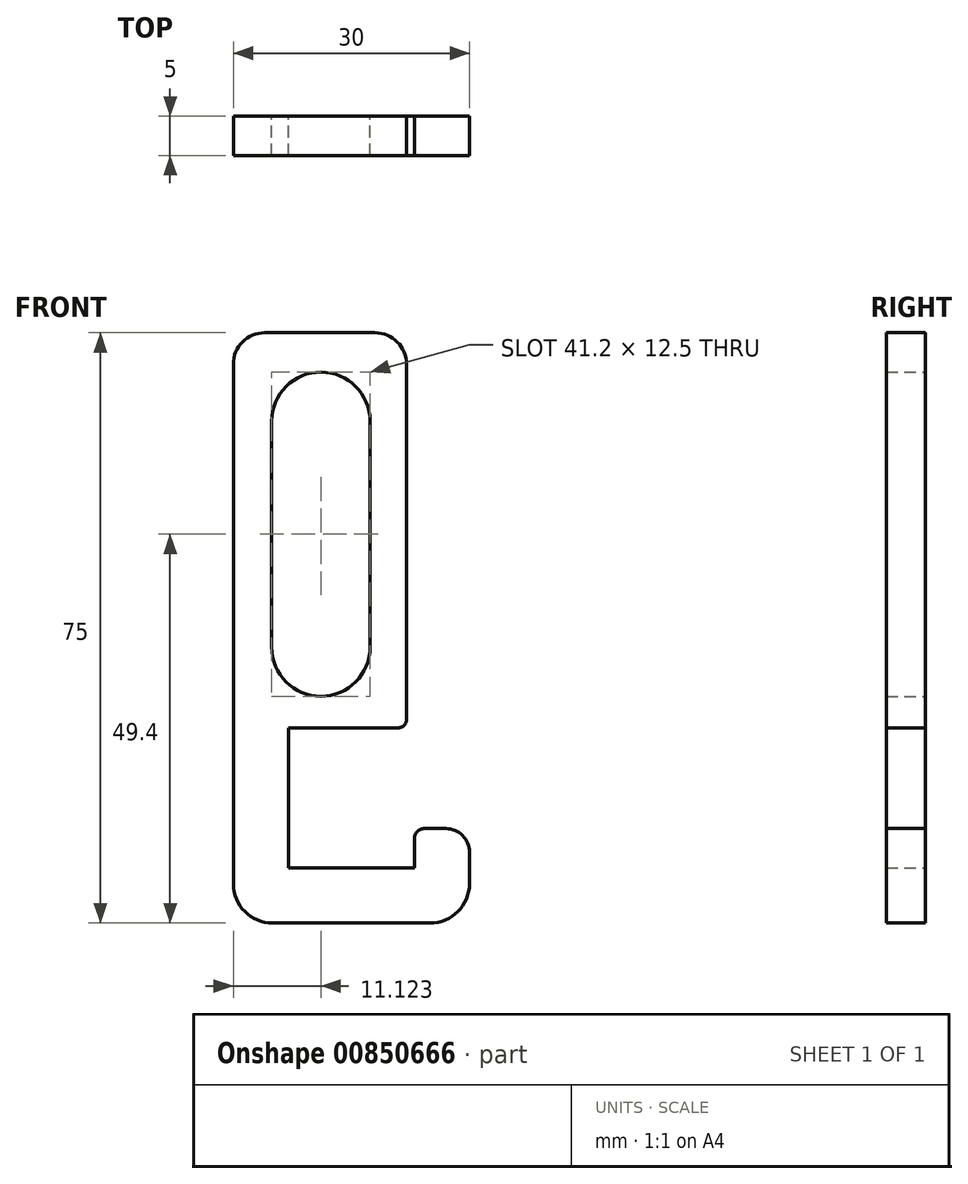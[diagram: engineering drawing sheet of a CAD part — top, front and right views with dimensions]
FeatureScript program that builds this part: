
annotation { "Feature Type Name" : "Feature", "Feature Type Description" : "" }
export const myFeature = defineFeature(function(context is Context, id is Id, definition is map)
    precondition{}
    {
        {
            var Q0;
            Q0=qCreatedBy(makeId("Front.planeOp"),FACE);
            var sketch = newSketch(context, id + "F0", { "sketchPlane" : qUnion([Q0])});
            skLineSegment(sketch, "E0", {"start": v(-30, 71) * mm, "end": v(-30, 5) * mm});
            skLineSegment(sketch, "E1", {"start": v(-25, 0) * mm, "end": v(-5, 0) * mm});
            skLineSegment(sketch, "E2", {"start": v(0, 5) * mm, "end": v(0, 9) * mm});
            skLineSegment(sketch, "E3", {"start": v(-3, 12) * mm, "end": v(-5.74, 12) * mm});
            skLineSegment(sketch, "E4", {"start": v(-7, 10.74) * mm, "end": v(-7, 7) * mm});
            skLineSegment(sketch, "E5", {"start": v(-7, 7) * mm, "end": v(-23, 7) * mm});
            skLineSegment(sketch, "E6", {"start": v(-23, 7) * mm, "end": v(-23, 24.8) * mm});
            skLineSegment(sketch, "E7", {"start": v(-23, 24.8) * mm, "end": v(-9.06, 24.8) * mm});
            skLineSegment(sketch, "E8", {"start": v(-8, 25.86) * mm, "end": v(-8, 71) * mm});
            skLineSegment(sketch, "E9", {"start": v(-12, 75) * mm, "end": v(-26, 75) * mm});
            skLineSegment(sketch, "E10", {"start": v(-29.85, 17.85) * mm, "end": v(-27.76, 18.2) * mm});
            skPoint(sketch, "E11.visualSharp", {"position": v(-30, 0) * mm});
            skArc(sketch, "E11.filletArc", {"start": v(-30, 5) * mm, "mid": v(-28.54, 1.46) * mm, "end": v(-25, 0) * mm});
            skPoint(sketch, "E12.visualSharp", {"position": v(0, 0) * mm});
            skArc(sketch, "E12.filletArc", {"start": v(-5, 0) * mm, "mid": v(-1.46, 1.46) * mm, "end": v(0, 5) * mm});
            skPoint(sketch, "E13.visualSharp", {"position": v(0, 12) * mm});
            skArc(sketch, "E13.filletArc", {"start": v(0, 9) * mm, "mid": v(-0.88, 11.12) * mm, "end": v(-3, 12) * mm});
            skPoint(sketch, "E14.visualSharp", {"position": v(-7, 12) * mm});
            skArc(sketch, "E14.filletArc", {"start": v(-5.74, 12) * mm, "mid": v(-6.63, 11.63) * mm, "end": v(-7, 10.74) * mm});
            skPoint(sketch, "E15.visualSharp", {"position": v(-8, 24.8) * mm});
            skArc(sketch, "E15.filletArc", {"start": v(-9.06, 24.8) * mm, "mid": v(-8.31, 25.11) * mm, "end": v(-8, 25.86) * mm});
            skArc(sketch, "E16.filletArc", {"start": v(-26, 75) * mm, "mid": v(-28.83, 73.83) * mm, "end": v(-30, 71) * mm});
            skPoint(sketch, "E17.visualSharp", {"position": v(-8, 75) * mm});
            skArc(sketch, "E17.filletArc", {"start": v(-8, 71) * mm, "mid": v(-9.17, 73.83) * mm, "end": v(-12, 75) * mm});
            skArc(sketch, "E18", {"start": v(-12.63, 63.75) * mm, "mid": v(-18.88, 70) * mm, "end": v(-25.13, 63.75) * mm});
            skArc(sketch, "E19", {"start": v(-25.13, 35.05) * mm, "mid": v(-18.88, 28.8) * mm, "end": v(-12.63, 35.05) * mm});
            skLineSegment(sketch, "E20", {"start": v(-12.63, 63.75) * mm, "end": v(-12.63, 35.05) * mm});
            skLineSegment(sketch, "E21", {"start": v(-25.13, 63.75) * mm, "end": v(-25.13, 35.05) * mm});
            skSolve(sketch);
        }
        {
            var Q0;
            Q0 = qSketchRegion(id + "F0", true);
            extrude(context, id + "F1", {"entities" : qUnion([Q0]), "depth" : 4 * mm, "offsetDistance" : 25 * mm});
        }
        {
            var Q0;
            Q0 = qSketchRegion(id + "F0", true);
            extrude(context, id + "F2", {"entities" : qUnion([Q0]), "operationType" : NewBodyOperationType.ADD, "depth" : 5 * mm, "offsetDistance" : 25 * mm});
        }
    });
